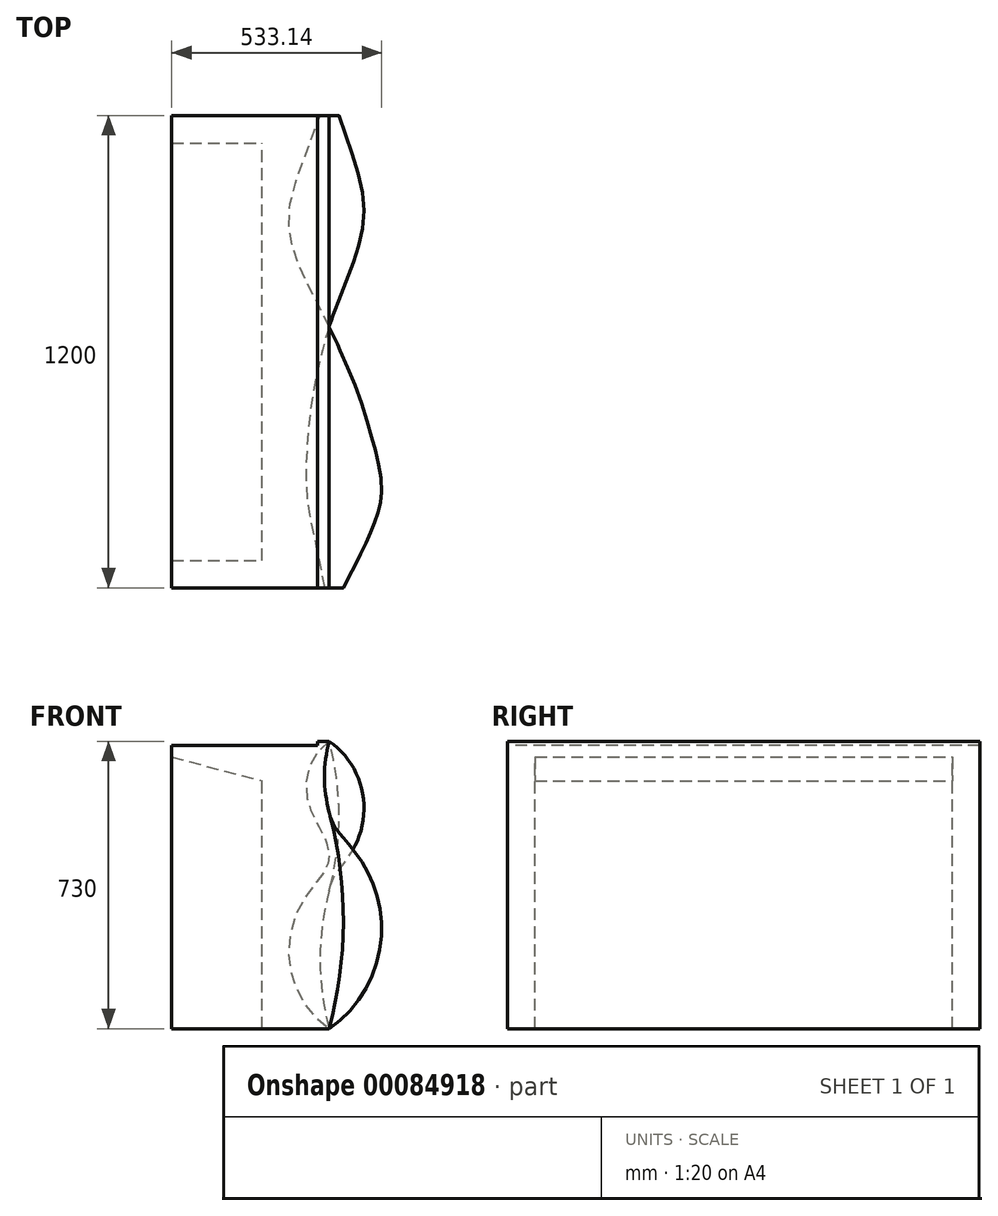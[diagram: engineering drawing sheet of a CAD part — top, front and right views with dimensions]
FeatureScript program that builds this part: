
annotation { "Feature Type Name" : "Feature", "Feature Type Description" : "" }
export const myFeature = defineFeature(function(context is Context, id is Id, definition is map)
    precondition{}
    {
        {
            assignVariable(context, id + "F0", {"name" : "Ecart", "anyValue" : 120});
        }
        {
            var Q0;
            Q0=qCreatedBy(makeId("Front.planeOp"),FACE);
            cPlane(context, id + "F1", {"entities" : qUnion([Q0]), "cplaneType" : CPlaneType.OFFSET, "offset" : (getVariable(context, 'Ecart')) * mm, "width" : 150 * mm, "height" : 150 * mm});
        }
        {
            var Q0;
            Q0=qCreatedBy(id+"F1.planeOp",FACE);
            cPlane(context, id + "F2", {"entities" : qUnion([Q0]), "cplaneType" : CPlaneType.OFFSET, "offset" : (getVariable(context, 'Ecart')) * mm, "width" : 150 * mm, "height" : 150 * mm});
        }
        {
            var Q0;
            Q0=qCreatedBy(id+"F2.planeOp",FACE);
            cPlane(context, id + "F3", {"entities" : qUnion([Q0]), "cplaneType" : CPlaneType.OFFSET, "offset" : (getVariable(context, 'Ecart')) * mm, "width" : 150 * mm, "height" : 150 * mm});
        }
        {
            var Q0;
            Q0=qCreatedBy(id+"F3.planeOp",FACE);
            cPlane(context, id + "F4", {"entities" : qUnion([Q0]), "cplaneType" : CPlaneType.OFFSET, "offset" : (getVariable(context, 'Ecart')) * mm, "width" : 150 * mm, "height" : 150 * mm});
        }
        {
            var Q0;
            Q0=qCreatedBy(id+"F4.planeOp",FACE);
            cPlane(context, id + "F5", {"entities" : qUnion([Q0]), "cplaneType" : CPlaneType.OFFSET, "offset" : (getVariable(context, 'Ecart')) * mm, "width" : 150 * mm, "height" : 150 * mm});
        }
        {
            var Q0;
            Q0=qCreatedBy(id+"F5.planeOp",FACE);
            cPlane(context, id + "F6", {"entities" : qUnion([Q0]), "cplaneType" : CPlaneType.OFFSET, "offset" : (getVariable(context, 'Ecart')) * mm, "width" : 150 * mm, "height" : 150 * mm});
        }
        {
            var Q0;
            Q0=qCreatedBy(id+"F6.planeOp",FACE);
            cPlane(context, id + "F7", {"entities" : qUnion([Q0]), "cplaneType" : CPlaneType.OFFSET, "offset" : (getVariable(context, 'Ecart')) * mm, "width" : 150 * mm, "height" : 150 * mm});
        }
        {
            var Q0;
            Q0=qCreatedBy(id+"F7.planeOp",FACE);
            cPlane(context, id + "F8", {"entities" : qUnion([Q0]), "cplaneType" : CPlaneType.OFFSET, "offset" : (getVariable(context, 'Ecart')) * mm, "width" : 150 * mm, "height" : 150 * mm});
        }
        {
            var Q0;
            Q0=qCreatedBy(id+"F8.planeOp",FACE);
            cPlane(context, id + "F9", {"entities" : qUnion([Q0]), "cplaneType" : CPlaneType.OFFSET, "offset" : (getVariable(context, 'Ecart')) * mm, "width" : 150 * mm, "height" : 150 * mm});
        }
        {
            var Q0;
            Q0=qCreatedBy(id+"F9.planeOp",FACE);
            cPlane(context, id + "F10", {"entities" : qUnion([Q0]), "cplaneType" : CPlaneType.OFFSET, "offset" : (getVariable(context, 'Ecart')) * mm, "width" : 150 * mm, "height" : 150 * mm});
        }
        {
            var Q0;
            Q0=qCreatedBy(makeId("Front.planeOp"),FACE);
            var sketch = newSketch(context, id + "F11", { "sketchPlane" : qUnion([Q0])});
            skLineSegment(sketch, "E0", {"start": v(400, 730) * mm, "end": v(0, 730) * mm});
            skLineSegment(sketch, "E1", {"start": v(0, 730) * mm, "end": v(0, 0) * mm});
            skLineSegment(sketch, "E2", {"start": v(0, 0) * mm, "end": v(400, 0) * mm});
            skLineSegment(sketch, "E3.bottom", {"start": v(0, 730) * mm, "end": v(610, 730) * mm, "construction": true});
            skLineSegment(sketch, "E3.top", {"start": v(0, 0) * mm, "end": v(610, 0) * mm, "construction": true});
            skLineSegment(sketch, "E3.left", {"start": v(0, 730) * mm, "end": v(0, 0) * mm, "construction": true});
            skLineSegment(sketch, "E3.right", {"start": v(610, 730) * mm, "end": v(610, 0) * mm, "construction": true});
            skLineSegment(sketch, "E4", {"start": v(300, 892.66) * mm, "end": v(300, -249.97) * mm, "construction": true});
            skPoint(sketch, "E5", {"position": v(305, 0) * mm});
            skArc(sketch, "E6", {"start": v(400, 0) * mm, "mid": v(376.96, 175) * mm, "end": v(400, 350) * mm});
            skArc(sketch, "E7", {"start": v(400, 350) * mm, "mid": v(425.01, 540) * mm, "end": v(400, 730) * mm});
            skLineSegment(sketch, "E8", {"start": v(-309.09, 540) * mm, "end": v(1053.1, 175) * mm, "construction": true});
            skLineSegment(sketch, "E9", {"start": v(1053.1, 175) * mm, "end": v(-331.13, 175) * mm, "construction": true});
            skSolve(sketch);
        }
        {
            var Q0;
            Q0=qCreatedBy(id+"F1.planeOp",FACE);
            var sketch = newSketch(context, id + "F12", { "sketchPlane" : qUnion([Q0])});
            skLineSegment(sketch, "E10", {"start": v(400, 730) * mm, "end": v(0, 730) * mm});
            skLineSegment(sketch, "E11", {"start": v(0, 730) * mm, "end": v(0, 0) * mm});
            skLineSegment(sketch, "E12", {"start": v(0, 0) * mm, "end": v(400, 0) * mm});
            skLineSegment(sketch, "E13.bottom", {"start": v(0, 730) * mm, "end": v(610, 730) * mm, "construction": true});
            skLineSegment(sketch, "E13.top", {"start": v(0, 0) * mm, "end": v(610, 0) * mm, "construction": true});
            skLineSegment(sketch, "E13.left", {"start": v(0, 730) * mm, "end": v(0, 0) * mm, "construction": true});
            skLineSegment(sketch, "E13.right", {"start": v(610, 730) * mm, "end": v(610, 0) * mm, "construction": true});
            skLineSegment(sketch, "E14", {"start": v(300, 955.35) * mm, "end": v(300, -187.3) * mm, "construction": true});
            skPoint(sketch, "E15", {"position": v(305, 0) * mm});
            skArc(sketch, "E16", {"start": v(400, 0) * mm, "mid": v(332.67, 185) * mm, "end": v(400, 370) * mm});
            skArc(sketch, "E17", {"start": v(400, 370) * mm, "mid": v(465.51, 550) * mm, "end": v(400, 730) * mm});
            skLineSegment(sketch, "E18", {"start": v(185.48, 550) * mm, "end": v(620.47, 185) * mm, "construction": true});
            skLineSegment(sketch, "E19", {"start": v(620.47, 185) * mm, "end": v(-367.48, 185) * mm, "construction": true});
            skSolve(sketch);
        }
        {
            var Q0;
            Q0=qCreatedBy(id+"F2.planeOp",FACE);
            var sketch = newSketch(context, id + "F13", { "sketchPlane" : qUnion([Q0])});
            skLineSegment(sketch, "E20", {"start": v(400, 730) * mm, "end": v(0, 730) * mm});
            skLineSegment(sketch, "E21", {"start": v(0, 730) * mm, "end": v(0, 0) * mm});
            skLineSegment(sketch, "E22", {"start": v(0, 0) * mm, "end": v(400, 0) * mm});
            skLineSegment(sketch, "E23.bottom", {"start": v(0, 730) * mm, "end": v(610, 730) * mm, "construction": true});
            skLineSegment(sketch, "E23.top", {"start": v(0, 0) * mm, "end": v(610, 0) * mm, "construction": true});
            skLineSegment(sketch, "E23.left", {"start": v(0, 730) * mm, "end": v(0, 0) * mm, "construction": true});
            skLineSegment(sketch, "E23.right", {"start": v(610, 730) * mm, "end": v(610, 0) * mm, "construction": true});
            skLineSegment(sketch, "E24", {"start": v(300, 1003.17) * mm, "end": v(300, -139.47) * mm, "construction": true});
            skPoint(sketch, "E25", {"position": v(305, 0) * mm});
            skArc(sketch, "E26", {"start": v(400, 0) * mm, "mid": v(298.49, 195) * mm, "end": v(400, 390) * mm});
            skArc(sketch, "E27", {"start": v(400, 390) * mm, "mid": v(488.5, 560) * mm, "end": v(400, 730) * mm});
            skLineSegment(sketch, "E28", {"start": v(280.96, 560) * mm, "end": v(536.54, 195) * mm, "construction": true});
            skLineSegment(sketch, "E29", {"start": v(536.54, 195) * mm, "end": v(-418.24, 195) * mm, "construction": true});
            skSolve(sketch);
        }
        {
            var Q0;
            Q0=qCreatedBy(id+"F3.planeOp",FACE);
            var sketch = newSketch(context, id + "F14", { "sketchPlane" : qUnion([Q0])});
            skLineSegment(sketch, "E30", {"start": v(400, 730) * mm, "end": v(0, 730) * mm});
            skLineSegment(sketch, "E31", {"start": v(0, 730) * mm, "end": v(0, 0) * mm});
            skLineSegment(sketch, "E32", {"start": v(0, 0) * mm, "end": v(400, 0) * mm});
            skLineSegment(sketch, "E33.bottom", {"start": v(0, 730) * mm, "end": v(610, 730) * mm, "construction": true});
            skLineSegment(sketch, "E33.top", {"start": v(0, 0) * mm, "end": v(610, 0) * mm, "construction": true});
            skLineSegment(sketch, "E33.left", {"start": v(0, 730) * mm, "end": v(0, 0) * mm, "construction": true});
            skLineSegment(sketch, "E33.right", {"start": v(610, 730) * mm, "end": v(610, 0) * mm, "construction": true});
            skLineSegment(sketch, "E34", {"start": v(300, 980.47) * mm, "end": v(300, -162.16) * mm, "construction": true});
            skPoint(sketch, "E35", {"position": v(305, 0) * mm});
            skArc(sketch, "E36", {"start": v(400, 0) * mm, "mid": v(315.09, 205) * mm, "end": v(400, 410) * mm});
            skArc(sketch, "E37", {"start": v(400, 410) * mm, "mid": v(466.27, 570) * mm, "end": v(400, 730) * mm});
            skLineSegment(sketch, "E38", {"start": v(240, 570) * mm, "end": v(605, 205) * mm, "construction": true});
            skLineSegment(sketch, "E39", {"start": v(605, 205) * mm, "end": v(-387.16, 205) * mm, "construction": true});
            skSolve(sketch);
        }
        {
            var Q0;
            Q0=qCreatedBy(id+"F4.planeOp",FACE);
            var sketch = newSketch(context, id + "F15", { "sketchPlane" : qUnion([Q0])});
            skLineSegment(sketch, "E40", {"start": v(400, 730) * mm, "end": v(0, 730) * mm});
            skLineSegment(sketch, "E41", {"start": v(0, 730) * mm, "end": v(0, 0) * mm});
            skLineSegment(sketch, "E42", {"start": v(0, 0) * mm, "end": v(400, 0) * mm});
            skLineSegment(sketch, "E43.bottom", {"start": v(0, 730) * mm, "end": v(610, 730) * mm, "construction": true});
            skLineSegment(sketch, "E43.top", {"start": v(0, 0) * mm, "end": v(610, 0) * mm, "construction": true});
            skLineSegment(sketch, "E43.left", {"start": v(0, 730) * mm, "end": v(0, 0) * mm, "construction": true});
            skLineSegment(sketch, "E43.right", {"start": v(610, 730) * mm, "end": v(610, 0) * mm, "construction": true});
            skLineSegment(sketch, "E44", {"start": v(300, 974.58) * mm, "end": v(300, -168.05) * mm, "construction": true});
            skPoint(sketch, "E45", {"position": v(305, 0) * mm});
            skArc(sketch, "E46", {"start": v(400, 0) * mm, "mid": v(371.7, 215) * mm, "end": v(400, 430) * mm});
            skArc(sketch, "E47", {"start": v(400, 430) * mm, "mid": v(419.75, 580) * mm, "end": v(400, 730) * mm});
            skLineSegment(sketch, "E48", {"start": v(-159.8, 580) * mm, "end": v(1202.4, 215) * mm, "construction": true});
            skLineSegment(sketch, "E49", {"start": v(1202.4, 215) * mm, "end": v(-395.06, 215) * mm, "construction": true});
            skSolve(sketch);
        }
        {
            var Q0;
            Q0=qCreatedBy(id+"F5.planeOp",FACE);
            var sketch = newSketch(context, id + "F16", { "sketchPlane" : qUnion([Q0])});
            skLineSegment(sketch, "E50", {"start": v(400, 730) * mm, "end": v(0, 730) * mm});
            skLineSegment(sketch, "E51", {"start": v(0, 730) * mm, "end": v(0, 0) * mm});
            skLineSegment(sketch, "E52", {"start": v(0, 0) * mm, "end": v(400, 0) * mm});
            skLineSegment(sketch, "E53.bottom", {"start": v(0, 730) * mm, "end": v(610, 730) * mm, "construction": true});
            skLineSegment(sketch, "E53.top", {"start": v(0, 0) * mm, "end": v(610, 0) * mm, "construction": true});
            skLineSegment(sketch, "E53.left", {"start": v(0, 730) * mm, "end": v(0, 0) * mm, "construction": true});
            skLineSegment(sketch, "E53.right", {"start": v(610, 730) * mm, "end": v(610, 0) * mm, "construction": true});
            skLineSegment(sketch, "E54", {"start": v(300, 815.54) * mm, "end": v(300, -327.1) * mm, "construction": true});
            skPoint(sketch, "E55", {"position": v(305, 0) * mm});
            skLineSegment(sketch, "E56", {"start": v(1476.68, 225) * mm, "end": v(-439.71, 225) * mm, "construction": true});
            skLineSegment(sketch, "E57", {"start": v(-439.71, 225) * mm, "end": v(922.49, 590) * mm, "construction": true});
            skArc(sketch, "E58", {"start": v(400, 450) * mm, "mid": v(381.57, 590) * mm, "end": v(400, 730) * mm});
            skArc(sketch, "E59", {"start": v(400, 450) * mm, "mid": v(429.62, 225) * mm, "end": v(400, 0) * mm});
            skLineSegment(sketch, "E60", {"start": v(400, 730) * mm, "end": v(400, 0) * mm, "construction": true});
            skSolve(sketch);
        }
        {
            var Q0;
            Q0=qCreatedBy(id+"F6.planeOp",FACE);
            var sketch = newSketch(context, id + "F17", { "sketchPlane" : qUnion([Q0])});
            skLineSegment(sketch, "E61", {"start": v(400, 730) * mm, "end": v(0, 730) * mm});
            skLineSegment(sketch, "E62", {"start": v(0, 730) * mm, "end": v(0, 0) * mm});
            skLineSegment(sketch, "E63", {"start": v(0, 0) * mm, "end": v(400, 0) * mm});
            skLineSegment(sketch, "E64.bottom", {"start": v(0, 730) * mm, "end": v(610, 730) * mm, "construction": true});
            skLineSegment(sketch, "E64.top", {"start": v(0, 0) * mm, "end": v(610, 0) * mm, "construction": true});
            skLineSegment(sketch, "E64.left", {"start": v(0, 730) * mm, "end": v(0, 0) * mm, "construction": true});
            skLineSegment(sketch, "E64.right", {"start": v(610, 730) * mm, "end": v(610, 0) * mm, "construction": true});
            skLineSegment(sketch, "E65", {"start": v(300, 702.63) * mm, "end": v(300, -440) * mm, "construction": true});
            skPoint(sketch, "E66", {"position": v(305, 0) * mm});
            skLineSegment(sketch, "E67", {"start": v(1045.66, 235) * mm, "end": v(88.14, 235) * mm, "construction": true});
            skLineSegment(sketch, "E68", {"start": v(88.14, 235) * mm, "end": v(572.52, 600) * mm, "construction": true});
            skArc(sketch, "E69", {"start": v(400, 470) * mm, "mid": v(356.5, 600) * mm, "end": v(400, 730) * mm});
            skArc(sketch, "E70", {"start": v(400, 470) * mm, "mid": v(478.63, 235) * mm, "end": v(400, 0) * mm});
            skLineSegment(sketch, "E71", {"start": v(400, 730) * mm, "end": v(400, 0) * mm, "construction": true});
            skSolve(sketch);
        }
        {
            var Q0;
            Q0=qCreatedBy(id+"F7.planeOp",FACE);
            var sketch = newSketch(context, id + "F18", { "sketchPlane" : qUnion([Q0])});
            skLineSegment(sketch, "E72", {"start": v(400, 730) * mm, "end": v(0, 730) * mm});
            skLineSegment(sketch, "E73", {"start": v(0, 730) * mm, "end": v(0, 0) * mm});
            skLineSegment(sketch, "E74", {"start": v(0, 0) * mm, "end": v(400, 0) * mm});
            skLineSegment(sketch, "E75.bottom", {"start": v(0, 730) * mm, "end": v(610, 730) * mm, "construction": true});
            skLineSegment(sketch, "E75.top", {"start": v(0, 0) * mm, "end": v(610, 0) * mm, "construction": true});
            skLineSegment(sketch, "E75.left", {"start": v(0, 730) * mm, "end": v(0, 0) * mm, "construction": true});
            skLineSegment(sketch, "E75.right", {"start": v(610, 730) * mm, "end": v(610, 0) * mm, "construction": true});
            skLineSegment(sketch, "E76", {"start": v(300, 631.88) * mm, "end": v(300, -510.76) * mm, "construction": true});
            skPoint(sketch, "E77", {"position": v(305, 0) * mm});
            skLineSegment(sketch, "E78", {"start": v(1297.5, 245) * mm, "end": v(194.42, 245) * mm, "construction": true});
            skLineSegment(sketch, "E79", {"start": v(194.42, 245) * mm, "end": v(500.7, 610) * mm, "construction": true});
            skArc(sketch, "E80", {"start": v(400, 490) * mm, "mid": v(344.04, 610) * mm, "end": v(400, 730) * mm});
            skArc(sketch, "E81", {"start": v(400, 490) * mm, "mid": v(514.25, 245) * mm, "end": v(400, 0) * mm});
            skLineSegment(sketch, "E82", {"start": v(400, 730) * mm, "end": v(400, 0) * mm, "construction": true});
            skSolve(sketch);
        }
        {
            var Q0;
            Q0=qCreatedBy(id+"F8.planeOp",FACE);
            var sketch = newSketch(context, id + "F19", { "sketchPlane" : qUnion([Q0])});
            skLineSegment(sketch, "E83", {"start": v(400, 730) * mm, "end": v(0, 730) * mm});
            skLineSegment(sketch, "E84", {"start": v(0, 730) * mm, "end": v(0, 0) * mm});
            skLineSegment(sketch, "E85", {"start": v(0, 0) * mm, "end": v(400, 0) * mm});
            skLineSegment(sketch, "E86.bottom", {"start": v(0, 730) * mm, "end": v(610, 730) * mm, "construction": true});
            skLineSegment(sketch, "E86.top", {"start": v(0, 0) * mm, "end": v(610, 0) * mm, "construction": true});
            skLineSegment(sketch, "E86.left", {"start": v(0, 730) * mm, "end": v(0, 0) * mm, "construction": true});
            skLineSegment(sketch, "E86.right", {"start": v(610, 730) * mm, "end": v(610, 0) * mm, "construction": true});
            skLineSegment(sketch, "E87", {"start": v(300, 665.92) * mm, "end": v(300, -476.72) * mm, "construction": true});
            skPoint(sketch, "E88", {"position": v(305, 0) * mm});
            skLineSegment(sketch, "E89", {"start": v(1467.22, 255) * mm, "end": v(221.45, 255) * mm, "construction": true});
            skLineSegment(sketch, "E90", {"start": v(221.45, 255) * mm, "end": v(477.02, 620) * mm, "construction": true});
            skArc(sketch, "E91", {"start": v(400, 510) * mm, "mid": v(342.74, 620) * mm, "end": v(400, 730) * mm});
            skArc(sketch, "E92", {"start": v(400, 510) * mm, "mid": v(532.74, 255) * mm, "end": v(400, 0) * mm});
            skLineSegment(sketch, "E93", {"start": v(400, 730) * mm, "end": v(400, 0) * mm, "construction": true});
            skSolve(sketch);
        }
        {
            var Q0;
            Q0=qCreatedBy(id+"F9.planeOp",FACE);
            var sketch = newSketch(context, id + "F20", { "sketchPlane" : qUnion([Q0])});
            skLineSegment(sketch, "E94", {"start": v(400, 730) * mm, "end": v(0, 730) * mm});
            skLineSegment(sketch, "E95", {"start": v(0, 730) * mm, "end": v(0, 0) * mm});
            skLineSegment(sketch, "E96", {"start": v(0, 0) * mm, "end": v(400, 0) * mm});
            skLineSegment(sketch, "E97.bottom", {"start": v(0, 730) * mm, "end": v(610, 730) * mm, "construction": true});
            skLineSegment(sketch, "E97.top", {"start": v(0, 0) * mm, "end": v(610, 0) * mm, "construction": true});
            skLineSegment(sketch, "E97.left", {"start": v(0, 730) * mm, "end": v(0, 0) * mm, "construction": true});
            skLineSegment(sketch, "E97.right", {"start": v(610, 730) * mm, "end": v(610, 0) * mm, "construction": true});
            skLineSegment(sketch, "E98", {"start": v(300, 849.58) * mm, "end": v(300, -293.06) * mm, "construction": true});
            skPoint(sketch, "E99", {"position": v(305, 0) * mm});
            skLineSegment(sketch, "E100", {"start": v(1542.21, 265) * mm, "end": v(84.19, 265) * mm, "construction": true});
            skLineSegment(sketch, "E101", {"start": v(84.19, 265) * mm, "end": v(519.18, 630) * mm, "construction": true});
            skArc(sketch, "E102", {"start": v(400, 530) * mm, "mid": v(363.6, 630) * mm, "end": v(400, 730) * mm});
            skArc(sketch, "E103", {"start": v(400, 530) * mm, "mid": v(496.45, 265) * mm, "end": v(400, 0) * mm});
            skLineSegment(sketch, "E104", {"start": v(400, 730) * mm, "end": v(400, 0) * mm, "construction": true});
            skSolve(sketch);
        }
        {
            var Q0;
            Q0=qCreatedBy(id+"F10.planeOp",FACE);
            var sketch = newSketch(context, id + "F21", { "sketchPlane" : qUnion([Q0])});
            skLineSegment(sketch, "E105", {"start": v(400, 730) * mm, "end": v(0, 730) * mm});
            skLineSegment(sketch, "E106", {"start": v(0, 730) * mm, "end": v(0, 0) * mm});
            skLineSegment(sketch, "E107", {"start": v(0, 0) * mm, "end": v(400, 0) * mm});
            skLineSegment(sketch, "E108.bottom", {"start": v(0, 730) * mm, "end": v(610, 730) * mm, "construction": true});
            skLineSegment(sketch, "E108.top", {"start": v(0, 0) * mm, "end": v(610, 0) * mm, "construction": true});
            skLineSegment(sketch, "E108.left", {"start": v(0, 730) * mm, "end": v(0, 0) * mm, "construction": true});
            skLineSegment(sketch, "E108.right", {"start": v(610, 730) * mm, "end": v(610, 0) * mm, "construction": true});
            skLineSegment(sketch, "E109", {"start": v(300, 856.84) * mm, "end": v(300, -285.8) * mm, "construction": true});
            skPoint(sketch, "E110", {"position": v(305, 0) * mm});
            skLineSegment(sketch, "E111", {"start": v(1846.8, 275) * mm, "end": v(-626.31, 275) * mm, "construction": true});
            skLineSegment(sketch, "E112", {"start": v(-626.31, 275) * mm, "end": v(735.88, 640) * mm, "construction": true});
            skArc(sketch, "E113", {"start": v(400, 550) * mm, "mid": v(388.15, 640) * mm, "end": v(400, 730) * mm});
            skArc(sketch, "E114", {"start": v(400, 550) * mm, "mid": v(436.2, 275) * mm, "end": v(400, 0) * mm});
            skLineSegment(sketch, "E115", {"start": v(400, 730) * mm, "end": v(400, 0) * mm, "construction": true});
            skSolve(sketch);
        }
        {
            var Q0;
            Q0 = qSketchRegion(id + "F11", true);
            var Q1;
            Q1 = qSketchRegion(id + "F12", true);
            var Q2;
            Q2 = qSketchRegion(id + "F13", true);
            var Q3;
            Q3 = qSketchRegion(id + "F14", true);
            var Q4;
            Q4 = qSketchRegion(id + "F15", true);
            var Q5;
            Q5 = qSketchRegion(id + "F16", true);
            var Q6;
            Q6 = qSketchRegion(id + "F17", true);
            var Q7;
            Q7 = qSketchRegion(id + "F18", true);
            var Q8;
            Q8 = qSketchRegion(id + "F19", true);
            var Q9;
            Q9 = qSketchRegion(id + "F20", true);
            var Q10;
            Q10 = qSketchRegion(id + "F21", true);
            loft(context, id + "F22", {"sheetProfilesArray" : [{ "sheetProfileEntities" : qUnion([Q0]) }, { "sheetProfileEntities" : qUnion([Q1]) }, { "sheetProfileEntities" : qUnion([Q2]) }, { "sheetProfileEntities" : qUnion([Q3]) }, { "sheetProfileEntities" : qUnion([Q4]) }, { "sheetProfileEntities" : qUnion([Q5]) }, { "sheetProfileEntities" : qUnion([Q6]) }, { "sheetProfileEntities" : qUnion([Q7]) }, { "sheetProfileEntities" : qUnion([Q8]) }, { "sheetProfileEntities" : qUnion([Q9]) }, { "sheetProfileEntities" : qUnion([Q10]) }]});
        }
        {
            var Q0;
            Q0=qCreatedBy(makeId("Front.planeOp"),FACE);
            cPlane(context, id + "F23", {"entities" : qUnion([Q0]), "cplaneType" : CPlaneType.OFFSET, "offset" : 70 * mm, "width" : 150 * mm, "height" : 150 * mm});
        }
        {
            var Q0;
            Q0=qCreatedBy(id+"F23.planeOp",FACE);
            var sketch = newSketch(context, id + "F24", { "sketchPlane" : qUnion([Q0])});
            skLineSegment(sketch, "E116.bottom", {"start": v(0, 0) * mm, "end": v(230, 0) * mm});
            skLineSegment(sketch, "E116.left", {"start": v(0, 0) * mm, "end": v(0, 690) * mm});
            skLineSegment(sketch, "E116.right", {"start": v(230, 0) * mm, "end": v(230, 630) * mm});
            skLineSegment(sketch, "E117", {"start": v(0, 690) * mm, "end": v(230, 630) * mm});
            skSolve(sketch);
        }
        {
            var Q0;
            Q0 = qSketchRegion(id + "F24", true);
            extrude(context, id + "F25", {"entities" : qUnion([Q0]), "operationType" : NewBodyOperationType.REMOVE, "depth" : 1060 * mm});
        }
        {
            var Q0;
            Q0=makeQuery(id+"F22.opLoft","CAP_FACE",FACE,{"disambiguationData":[OSD([makeQuery(id+"F11.imprint","IMPRINT",FACE,{"disambiguationData":[TD([[makeQuery(id+"F11.imprint","IMPRINT",EDGE,{"derivedFrom":sQuery(id+"F11.wireOp",EDGE,"E0")}),1.0]])]})])],"isStart":true});
            var sketch = newSketch(context, id + "F26", { "sketchPlane" : qUnion([Q0])});
            skLineSegment(sketch, "E118.bottom", {"start": v(-370, 730) * mm, "end": v(230, 730) * mm});
            skLineSegment(sketch, "E118.top", {"start": v(-370, 720) * mm, "end": v(230, 720) * mm});
            skLineSegment(sketch, "E118.left", {"start": v(-370, 730) * mm, "end": v(-370, 720) * mm});
            skLineSegment(sketch, "E118.right", {"start": v(230, 730) * mm, "end": v(230, 720) * mm});
            skSolve(sketch);
        }
        {
            var Q0;
            Q0 = qSketchRegion(id + "F26", true);
            var Q1;
            Q1=makeQuery(id+"F22.opLoft","CAP_FACE",FACE,{"disambiguationData":[OSD([makeQuery(id+"F21.imprint","IMPRINT",FACE,{"disambiguationData":[TD([[makeQuery(id+"F21.imprint","IMPRINT",EDGE,{"derivedFrom":sQuery(id+"F21.wireOp",EDGE,"E105")}),1.0]])]})])],"isStart":true});
            extrude(context, id + "F27", {"entities" : qUnion([Q0]), "operationType" : NewBodyOperationType.REMOVE, "endBound" : BoundingType.UP_TO_SURFACE, "oppositeDirection" : true, "endBoundEntityFace" : qUnion([Q1]), "depth" : 25 * mm});
        }
    });
